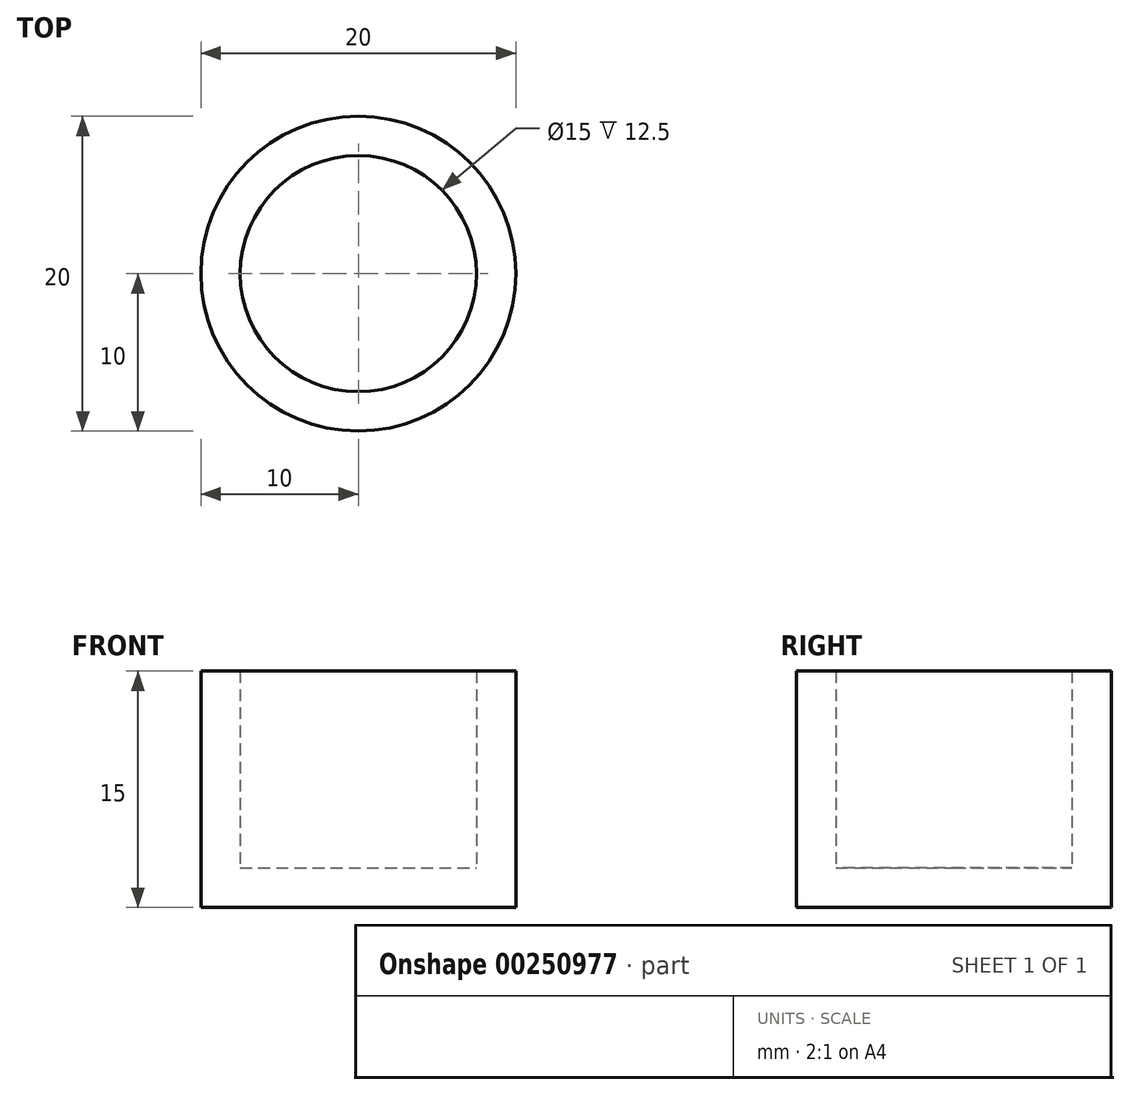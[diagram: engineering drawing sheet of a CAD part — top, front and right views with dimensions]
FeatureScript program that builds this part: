
annotation { "Feature Type Name" : "Feature", "Feature Type Description" : "" }
export const myFeature = defineFeature(function(context is Context, id is Id, definition is map)
    precondition{}
    {
        {
            var Q0;
            Q0=qCreatedBy(makeId("Front.planeOp"),FACE);
            var sketch = newSketch(context, id + "F0", { "sketchPlane" : qUnion([Q0])});
            skLineSegment(sketch, "E0.bottom", {"start": v(10, 7.5) * mm, "end": v(-10, 7.5) * mm});
            skLineSegment(sketch, "E0.top", {"start": v(10, -7.5) * mm, "end": v(-10, -7.5) * mm});
            skLineSegment(sketch, "E0.left", {"start": v(10, 7.5) * mm, "end": v(10, -7.5) * mm});
            skLineSegment(sketch, "E0.right", {"start": v(-10, 7.5) * mm, "end": v(-10, -7.5) * mm});
            skPoint(sketch, "E0.middle", {"position": v(0, 0) * mm});
            skLineSegment(sketch, "E1", {"start": v(0, 7.5) * mm, "end": v(0, -7.5) * mm});
            skLineSegment(sketch, "E2", {"start": v(0, -7.5) * mm, "end": v(0, 7.5) * mm});
            skSolve(sketch);
        }
        {
            var Q0;
            {var subQ0=sQuery(id+"F0.wireOp",EDGE,"E0.right");Q0=makeQuery(id+"F0.imprint","IMPRINT",FACE,{"disambiguationData":[TD([[makeQuery(id+"F0.imprint","IMPRINT",EDGE,{"derivedFrom":subQ0}),1.0]])]});}
            var Q1;
            Q1=sQuery(id+"F0.wireOp",EDGE,"E2");
            revolve(context, id + "F1", {"entities" : qUnion([Q0]), "axis" : qUnion([Q1]), "revolveType" : RevolveType.FULL});
        }
        {
            var Q0;
            Q0=makeQuery(id+"F1.opRevolve","SWEPT_FACE",FACE,{"disambiguationData":[OSD([sQuery(id+"F0.wireOp",EDGE,"E0.bottom")])]});
            shell(context, id + "F2", {"entities" : qUnion([Q0]), "thickness" : 2.5 * mm});
        }
    });
